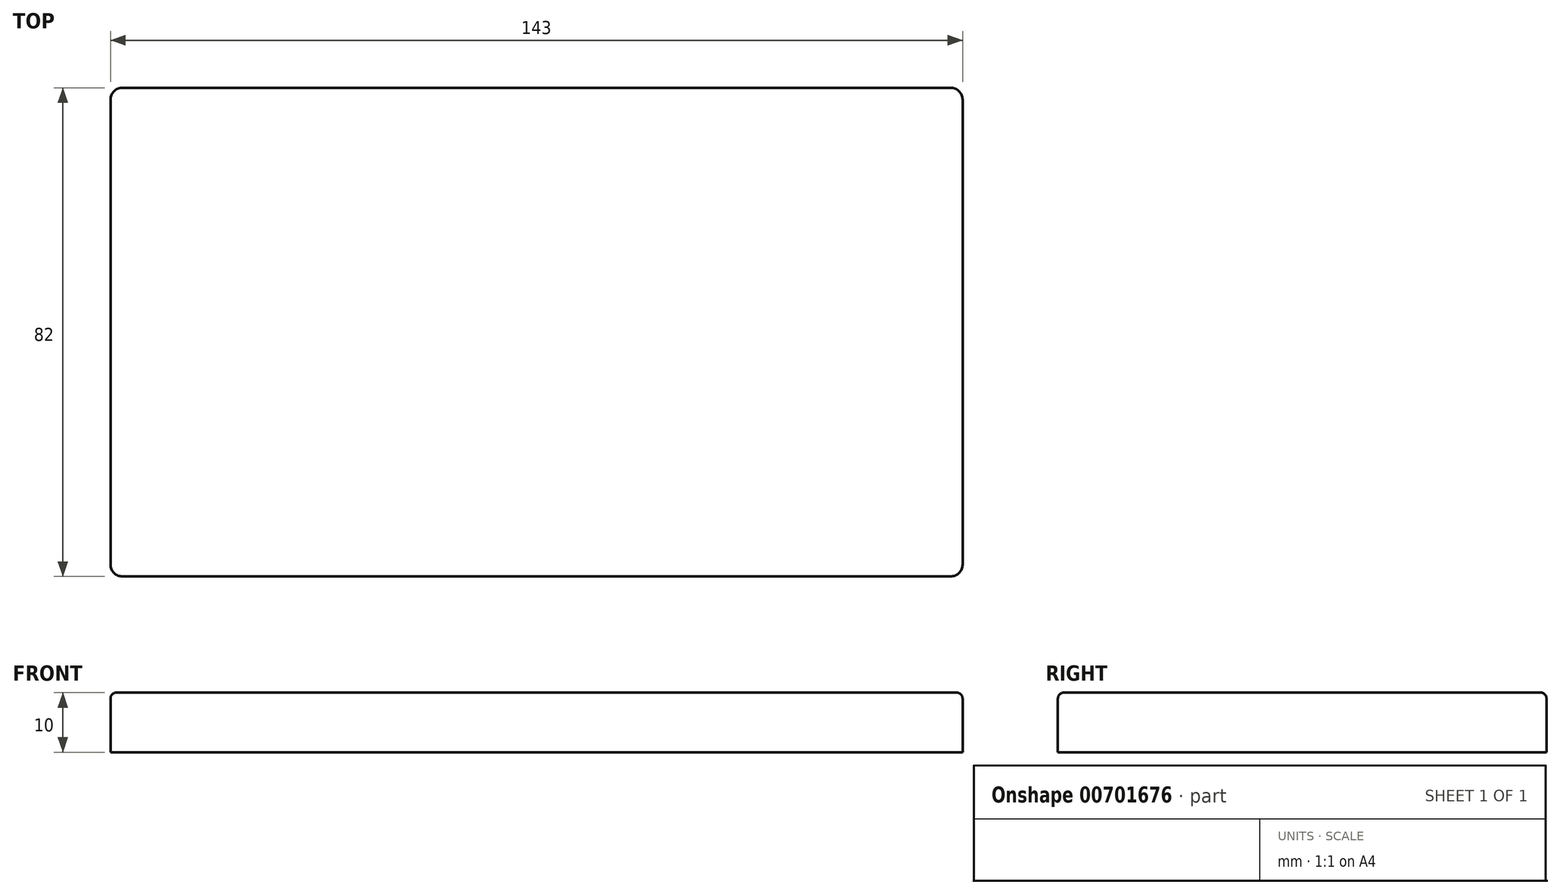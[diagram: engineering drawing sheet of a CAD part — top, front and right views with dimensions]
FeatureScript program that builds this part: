
annotation { "Feature Type Name" : "Feature", "Feature Type Description" : "" }
export const myFeature = defineFeature(function(context is Context, id is Id, definition is map)
    precondition{}
    {
        {
            var Q0;
            Q0=qCreatedBy(makeId("Top.planeOp"),FACE);
            var sketch = newSketch(context, id + "F0", { "sketchPlane" : qUnion([Q0]), "disableImprinting" : false});
            skLineSegment(sketch, "E0.bottom", {"start": v(-69.5, 41) * mm, "end": v(69.5, 41) * mm});
            skLineSegment(sketch, "E0.top", {"start": v(-69.5, -41) * mm, "end": v(69.5, -41) * mm});
            skLineSegment(sketch, "E0.left", {"start": v(-71.5, 39) * mm, "end": v(-71.5, -39) * mm});
            skLineSegment(sketch, "E0.right", {"start": v(71.5, 39) * mm, "end": v(71.5, -39) * mm});
            skPoint(sketch, "E0.middle", {"position": v(0, 0) * mm});
            skPoint(sketch, "E1.visualSharp", {"position": v(-71.5, 41) * mm});
            skArc(sketch, "E1.filletArc", {"start": v(-69.5, 41) * mm, "mid": v(-70.91, 40.41) * mm, "end": v(-71.5, 39) * mm});
            skPoint(sketch, "E2.visualSharp", {"position": v(71.5, 41) * mm});
            skArc(sketch, "E2.filletArc", {"start": v(71.5, 39) * mm, "mid": v(70.91, 40.41) * mm, "end": v(69.5, 41) * mm});
            skPoint(sketch, "E3.visualSharp", {"position": v(-71.5, -41) * mm});
            skArc(sketch, "E3.filletArc", {"start": v(-71.5, -39) * mm, "mid": v(-70.91, -40.41) * mm, "end": v(-69.5, -41) * mm});
            skPoint(sketch, "E4.visualSharp", {"position": v(71.5, -41) * mm});
            skArc(sketch, "E4.filletArc", {"start": v(69.5, -41) * mm, "mid": v(70.91, -40.41) * mm, "end": v(71.5, -39) * mm});
            skSolve(sketch);
        }
        {
            var Q0;
            Q0=makeQuery(id+"F0.imprint","IMPRINT",FACE,{"disambiguationData":[TD([[makeQuery(id+"F0.imprint","IMPRINT",EDGE,{"derivedFrom":sQuery(id+"F0.wireOp",EDGE,"E0.bottom")}),-1.0]])]});
            extrude(context, id + "F1", {"entities" : qUnion([Q0]), "depth" : 10 * mm, "offsetDistance" : 25 * mm});
        }
        {
            var Q0;
            Q0=makeQuery(id+"F1.opExtrude","CAP_EDGE",EDGE,{"disambiguationData":[OSD([sQuery(id+"F0.wireOp",EDGE,"E0.top")])],"isStart":false});
            fillet(context, id + "F2", {"entities" : qUnion([Q0]), "radius" : 1 * mm, "tangentPropagation" : true, "allowEdgeOverflow" : false});
        }
    });
